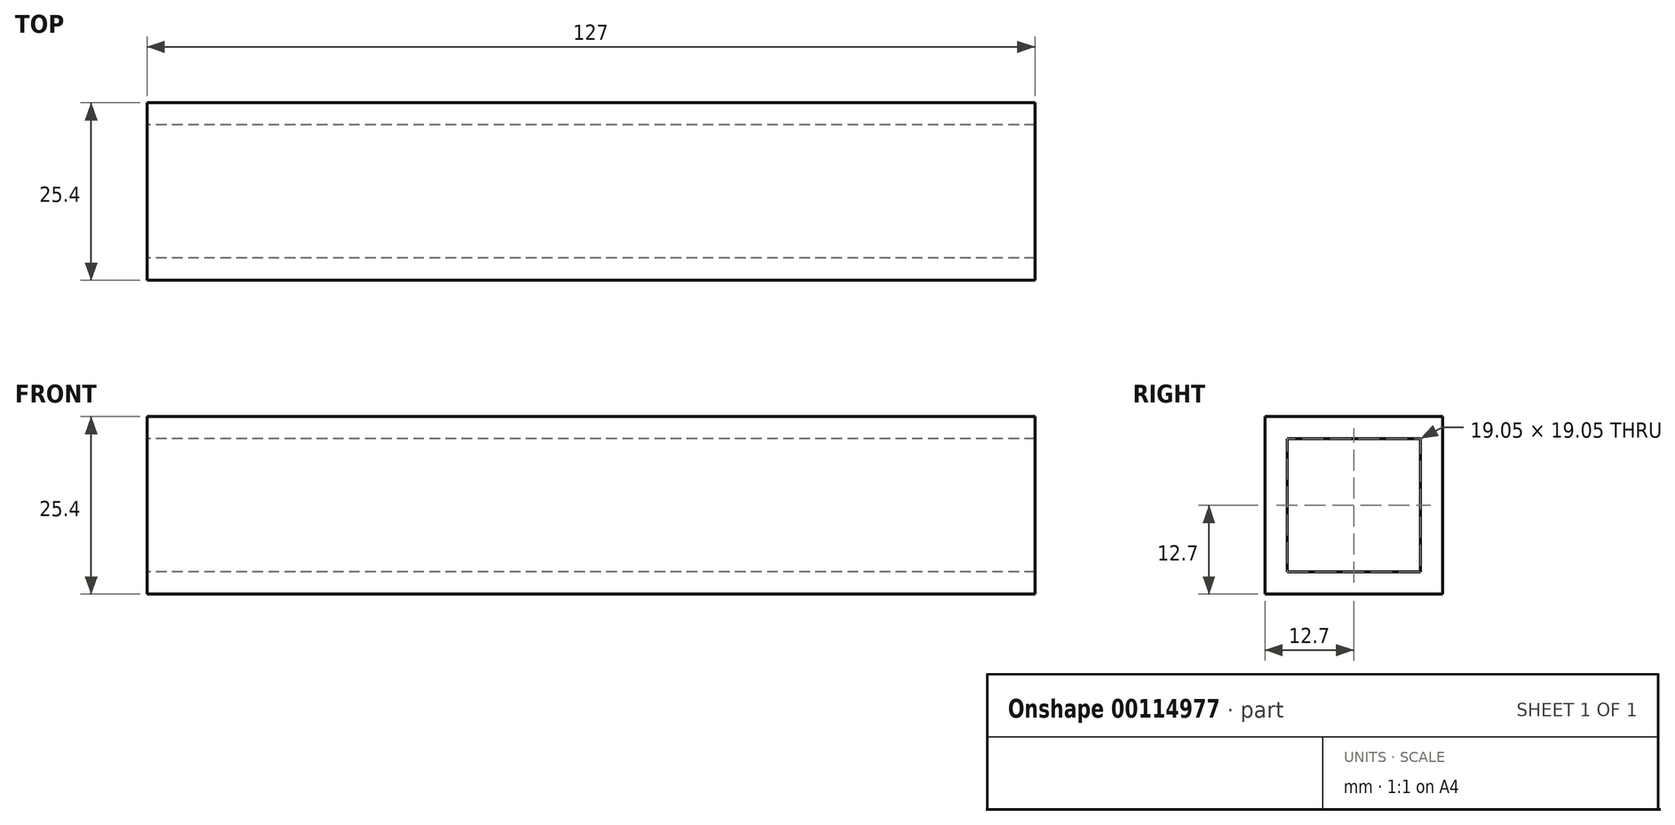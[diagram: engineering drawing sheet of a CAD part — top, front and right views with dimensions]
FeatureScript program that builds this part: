
annotation { "Feature Type Name" : "Feature", "Feature Type Description" : "" }
export const myFeature = defineFeature(function(context is Context, id is Id, definition is map)
    precondition{}
    {
        {
            var Q0;
            Q0=qCreatedBy(makeId("Right.planeOp"),FACE);
            var sketch = newSketch(context, id + "F0", { "sketchPlane" : qUnion([Q0])});
            skLineSegment(sketch, "E0.bottom", {"start": v(-25.4, 25.4) * mm, "end": v(0, 25.4) * mm});
            skLineSegment(sketch, "E0.top", {"start": v(-25.4, 0) * mm, "end": v(0, 0) * mm});
            skLineSegment(sketch, "E0.left", {"start": v(-25.4, 25.4) * mm, "end": v(-25.4, 0) * mm});
            skLineSegment(sketch, "E0.right", {"start": v(0, 25.4) * mm, "end": v(0, 0) * mm});
            skLineSegment(sketch, "E1.bottom", {"start": v(-22.23, 22.23) * mm, "end": v(-3.17, 22.23) * mm});
            skLineSegment(sketch, "E1.top", {"start": v(-22.23, 3.18) * mm, "end": v(-3.17, 3.18) * mm});
            skLineSegment(sketch, "E1.left", {"start": v(-22.23, 22.23) * mm, "end": v(-22.23, 3.18) * mm});
            skLineSegment(sketch, "E1.right", {"start": v(-3.17, 22.23) * mm, "end": v(-3.17, 3.18) * mm});
            skSolve(sketch);
        }
        {
            var Q0;
            Q0=makeQuery(id+"F0.imprint","IMPRINT",FACE,{"disambiguationData":[TD([[makeQuery(id+"F0.imprint","IMPRINT",EDGE,{"derivedFrom":sQuery(id+"F0.wireOp",EDGE,"E0.bottom")}),-1.0]])]});
            extrude(context, id + "F1", {"entities" : qUnion([Q0]), "depth" : 127 * mm});
        }
    });
